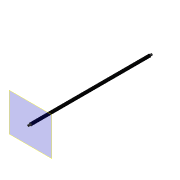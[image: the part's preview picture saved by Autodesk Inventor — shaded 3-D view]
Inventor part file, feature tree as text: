
AUTODESK INVENTOR PART (.ipt)
format: ipt  version: 2016 (Build 200138000, 138)  size: 98,816 bytes
history: native  units: mm
features: extrude x5, sketch x5, thread x2, chamfer x2, plane x1
ambient origin geometry x8: Origin, YZ Plane, XZ Plane, XY Plane, X Axis, Y Axis, Z Axis, Center Point
bodies: Body1 (feature_tree)
feature tree (15):
  plane  "Work Plane1"
  extrude  "Extrusion1"  Depth=3.0mm
  extrude  "Extrusion2"  Depth=3.0mm
  extrude  "Extrusion3"  Depth=10.0mm
  thread  "Thread1"  [1 undecoded]
  chamfer  "Chamfer2"  Distance=10.0mm
  extrude  "Extrusion4"  Depth=3.0mm
  extrude  "Extrusion5"  Depth=2.0mm
  thread  "Thread2"  [1 undecoded]
  chamfer  "Chamfer3"  Distance=10.0mm
  sketch  "Sketch2"  dims[d4=3.0mm d6=6.0mm]
  sketch  "Sketch5"  dims[d7=251.0mm d8=0.0mm d26=3.0mm]
  sketch  "Sketch6"  dims[d27=4.7mm d28=0.0mm d29=4.0mm d30=3.7mm d31=0.0mm d32=10.0mm d33=0.0mm]
  sketch  "Sketch7"  dims[d34=0.3mm d35=2.0mm d36=45.0deg d37=3.0mm]
  sketch  "Sketch8"  dims[d38=4.7mm d39=0.0mm d40=4.0mm d41=3.7mm d42=0.0mm d43=10.0mm d44=0.0mm d45=0.3mm d46=2.0mm d47=45.0deg]
note: 2 required parameter values undecoded (feature->parameter linkage not recoverable at this tier; creation-order binding heuristic only, values carry confidence <= 0.55)
